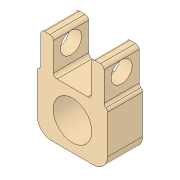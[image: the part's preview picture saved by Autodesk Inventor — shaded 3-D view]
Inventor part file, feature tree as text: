
AUTODESK INVENTOR PART (.ipt)
format: ipt  version: 2018.3 (Build 223284000, 284)  size: 293,888 bytes
history: native  units: in
note: dims shown in document units (in); Inventor stores cm internally (conversion verified against a paired STEP export)
features: extrude x3, fillet x3, sketch x3
ambient origin geometry x8: Origin, YZ Plane, XZ Plane, XY Plane, X Axis, Y Axis, Z Axis, Center Point
bodies: Solid1 (feature_tree)
feature tree (9):
  extrude  "Extrusion1"  Depth=0.625in TaperAngle=0.0deg
  extrude  "Extrusion2"  Depth=0.625in TaperAngle=0.0deg
  extrude  "Extrusion3"  Depth=0.625in TaperAngle=0.0deg
  fillet  "Fillet1"  Radius=0.0625in
  fillet  "Fillet2"  Radius=0.0625in
  fillet  "Fillet3"  Radius=0.25in
  sketch  "Sketch1"  dims[d0=1.0in d1=0.225in d2=0.225in d3=0.625in d4=1.25in d5=0.0625in d6=0.0625in d7=0.675in d8=0.625in d9=0.0in]
  sketch  "Sketch2"  dims[d10=0.6885in d13=0.5in d14=0.625in d15=0.0in]
  sketch  "Sketch3"  dims[d16=0.375in d17=0.25in d18=0.0in d19=0.625in d20=0.0in d21=0.0625in d22=0.0625in d23=0.25in]
